# Revit family: QF_VOLLRATH_36429R
name_source: partatom
category: Specialty Equipment
revit_build: Autodesk Revit 2016 (Build: 20150220_1215(x64)
units: mm (PartAtom-declared; Revit-internal decimal feet)

## family parameters
Always vertical = Yes
Cut with Voids When Loaded = Yes
OmniClass Number = 23.40.40.14.24.14
OmniClass Title = Service Line Equipment
Part Type = Normal
Room Calculation Point = No
Round Connector Dimension = Use Diameter
Shared = No
Work Plane-Based = Yes

## types (1)
- 36429R
    Assembly Code = E1090320
    BTUH = 1500.0 Btu/h
    Default Elevation = 0"
    Description = TWO-WELL NSF 7-CERTIFIED REMOTE REFRIGERATED DROP-IN COLD WELL
    Direct Waste Connection Height = 0"
    Direct Waste Flow = 0 GPM
    Direct Waste RI Height = 0"
    Direct Waste Size = 1"
    Manufacturer = VOLLRATH US
    Model = 36429R
    Refrigerant Volume = 0.00 kip
    URL = www.vollrathfoodservice.com
    URL Cutsheet = www.vollrathfoodservice.com/downloads/59738/SPCDrop-inRemoteRefrigNSF7StndrdColdPanL35708en2013-07-30-pdf
    Weight in Pounds = 0

## geometry (parser evidence)
native form markers: Sweep x2
no freeform markers — native parametric forms only
